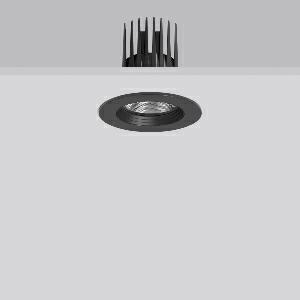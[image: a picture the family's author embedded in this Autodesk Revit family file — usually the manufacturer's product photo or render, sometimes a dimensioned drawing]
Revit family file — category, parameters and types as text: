
# Revit family: heledon_mini_e_901740_003_867f
name_source: partatom
category: Lighting Fixtures
units: mm (PartAtom-declared; Revit-internal decimal feet)

## family parameters
Cut with Voids When Loaded = No
Host = Face
Light Source = No
Part Type = Normal
Room Calculation Point = No
Round Connector Dimension = Use Diameter
Shared = No

## types (1)
- HELEDON mini E (1 x LED Modul 930, 2500 lm, 3000)
    Apparent Load = 20 VA
    Approval mark = CE
    CIE Flux Codes = 100 100 100 100 100
    Color Rendering = 90
    Color Temperature = 3000
    Default Elevation = 1800 mm
    Description = Series: HELEDON mini
Round recessed downlight. Housing: die-cast aluminium, powder-coated. Black plastic ring and recessed LED to prevent glare from the side. Optical assembly with reflector made of MIRO-Silver with 98% total light reflection for outstanding efficiency - can be changed without tools. Best colour rendering index Ra>90. Suitable for Recessed ceiling mounting. Installation without tools thanks to spring fastening system. Including separate LED converter with connecting cable 600 mm.High quality converter without flickering and stroboscopic effect. Through-wiring box (5 pole) available as accessory. The following accessories can be mounted without use of tools: interchangeable lenses, decorative glasses, honeycomb louvre, clear and frosted diffusers, white interchangeable plastic ring. 
Colour: deep black, matt (RAL 9005)
Diameter: 124 mm
Height: 3 mm
Cut-out diameter: 114 mm
Recess height: 170 mm
Luminaire: recess height: 120 mm
Lamp: LED
Socket: without socket
Colour temperature: 3000K
Colour rendering index (CRI): 92
System power: 20 W
Rated luminous flux: 2500 lm
Luminous efficiency: 125 lm/W
Control gear: Regulated power supply
Protection class: II
Type of protection: IP 20
    Height = 0 mm  [stored 0 ft]
    Lamp = 1 x LED Modul 930
    Lamp Light Flux = 2500 lm
    Lamp count = 1
    Length = 124 mm  [stored 0.406824 ft]
    Lifetime = 50000 h
    Luminous efficacy = 125 lm/W
    Manufacturer = RZB
    ModVariant = No
    Model = 901740.003
    Mounting Place = Ceiling
    Mounting Type = Recessed
    Number of Poles = 1
    OnlyDefault = Yes
    Power Factor = 1
    Product Name = HELEDON mini E
    Product group = Recessed downlights
    ProductGroupID = 402
    Protection Class = Protection class II
    Protection Degree = IP 20
    RLX_Detail_Level = 1
    RLX_Emergency_Light_Flux = 0 lm
    RLX_Emergency_Type = 0
    RLX_Emergency_Type_DB = No
    RlxData = <blob elided: 126121 chars, md5=633b4c36>
    Socket = socket
    Standby Power = 0 W
    System Light Flux = 2500 lm
    System Power = 20 W
    Type Comments = Product without accessories
    Type Image = 901657.003.jpg
    URL = http://relux.com
    VarID = ---
    Voltage = 230 V
    Voltage Range = 220-240 V
    Weight = 0.00 kg
    Width = 0 mm  [stored 0 ft]

note: [stored X ft] marks values corroborated as IEEE doubles in the binary element streams (Revit-internal decimal feet)

## geometry (parser evidence)
native form markers: Blend x4, Sweep x10
no freeform markers — native parametric forms only
